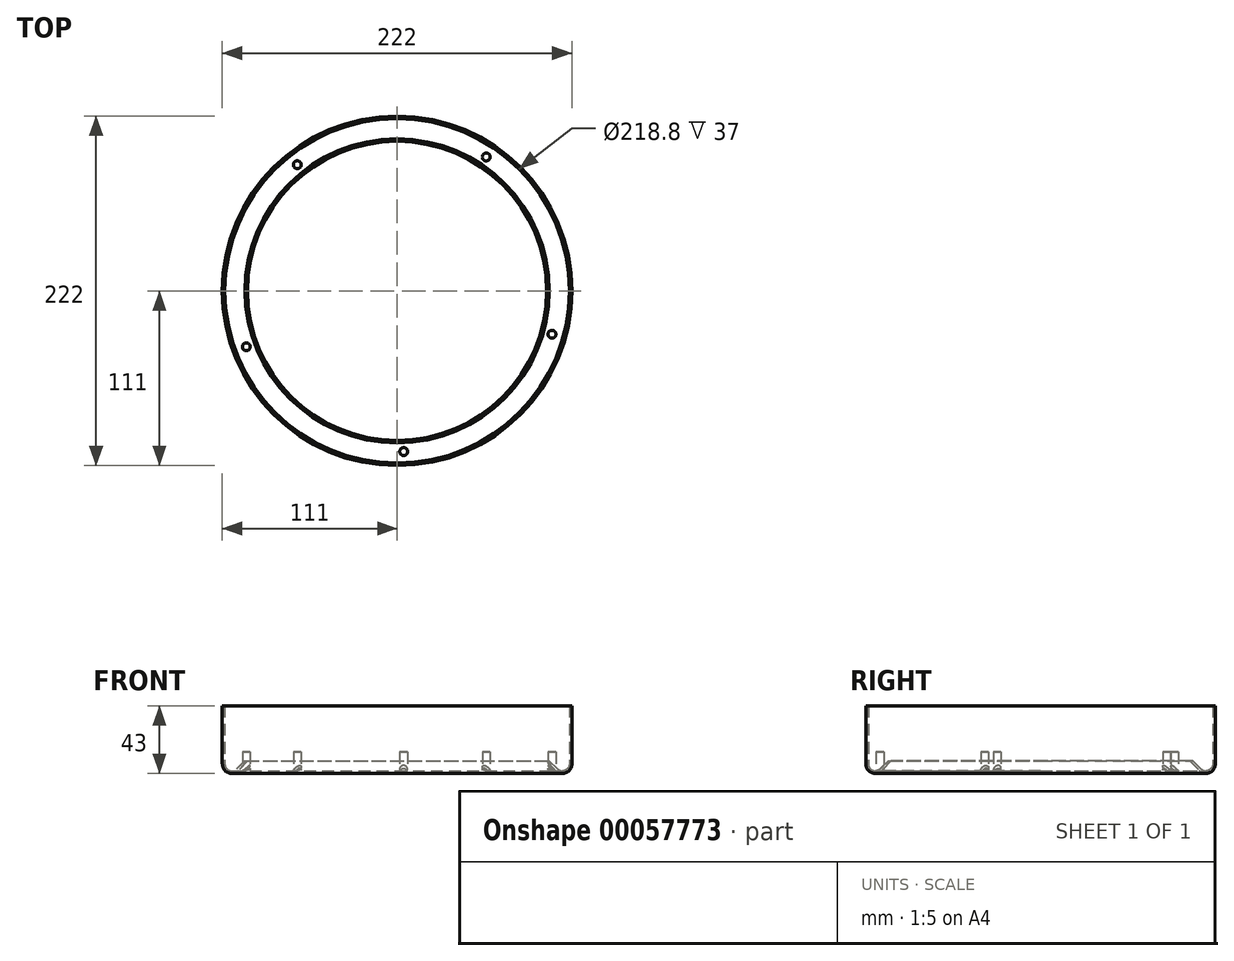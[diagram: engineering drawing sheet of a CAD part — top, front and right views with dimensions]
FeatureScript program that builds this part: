
annotation { "Feature Type Name" : "Feature", "Feature Type Description" : "" }
export const myFeature = defineFeature(function(context is Context, id is Id, definition is map)
    precondition{}
    {
        {
            var Q0;
            Q0=qCreatedBy(makeId("Front.planeOp"),FACE);
            var sketch = newSketch(context, id + "F0", { "sketchPlane" : qUnion([Q0])});
            skLineSegment(sketch, "E0", {"start": v(0, 0) * mm, "end": v(0, 29.4) * mm});
            skLineSegment(sketch, "E1.0", {"start": v(111, 6.44) * mm, "end": v(111, 43.44) * mm});
            skLineSegment(sketch, "E2.0", {"start": v(95, 8.44) * mm, "end": v(96.6, 8.44) * mm});
            skLineSegment(sketch, "E3.0", {"start": v(109.4, 6.44) * mm, "end": v(109.4, 43.44) * mm});
            skArc(sketch, "E4.filletArc", {"start": v(105, 2.04) * mm, "mid": v(108.11, 3.33) * mm, "end": v(109.4, 6.44) * mm});
            skArc(sketch, "E5.filletArc", {"start": v(105, 0.44) * mm, "mid": v(109.24, 2.2) * mm, "end": v(111, 6.44) * mm});
            skArc(sketch, "E6.MirrorCS", {"start": v(105, 2.04) * mm, "mid": v(103.35, 2.36) * mm, "end": v(101.94, 3.27) * mm});
            skArc(sketch, "E7.MirrorCS", {"start": v(105, 0.44) * mm, "mid": v(102.6, 0.94) * mm, "end": v(100.59, 2.37) * mm});
            skLineSegment(sketch, "E8", {"start": v(95, 8.44) * mm, "end": v(100.59, 2.37) * mm});
            skLineSegment(sketch, "E9", {"start": v(96.6, 8.44) * mm, "end": v(101.94, 3.27) * mm});
            skLineSegment(sketch, "E10", {"start": v(111, 43.44) * mm, "end": v(109.4, 43.44) * mm});
            skSolve(sketch);
        }
        {
            var Q0;
            Q0=makeQuery(id+"F0.imprint","IMPRINT",FACE,{"disambiguationData":[TD([[makeQuery(id+"F0.imprint","IMPRINT",EDGE,{"derivedFrom":sQuery(id+"F0.wireOp",EDGE,"E1.0")}),1.0]])]});
            var Q1;
            Q1=sQuery(id+"F0.wireOp",EDGE,"E0");
            revolve(context, id + "F1", {"entities" : qUnion([Q0]), "axis" : qUnion([Q1]), "revolveType" : RevolveType.FULL});
        }
        {
            var Q0;
            Q0=qCreatedBy(makeId("Top.planeOp"),FACE);
            var sketch = newSketch(context, id + "F2", { "sketchPlane" : qUnion([Q0])});
            skCircle(sketch, "E11.cCircle", {"center": v(0, 0) * mm, "radius": 102.16 * mm, "construction": true});
            skLineSegment(sketch, "E11.0", {"start": v(56.61, 85.04) * mm, "end": v(98.38, -27.56) * mm});
            skLineSegment(sketch, "E11.1", {"start": v(98.38, -27.56) * mm, "end": v(4.19, -102.08) * mm});
            skLineSegment(sketch, "E11.2", {"start": v(4.19, -102.08) * mm, "end": v(-95.79, -35.53) * mm});
            skLineSegment(sketch, "E11.3", {"start": v(-95.79, -35.53) * mm, "end": v(-63.39, 80.12) * mm});
            skLineSegment(sketch, "E11.4", {"start": v(-63.39, 80.12) * mm, "end": v(56.61, 85.04) * mm});
            skCircle(sketch, "E12", {"center": v(56.61, 85.04) * mm, "radius": 2.5 * mm});
            skCircle(sketch, "E13.1.0", {"center": v(-63.39, 80.12) * mm, "radius": 2.5 * mm});
            skCircle(sketch, "E13.2.0", {"center": v(-95.79, -35.53) * mm, "radius": 2.5 * mm});
            skCircle(sketch, "E13.3.0", {"center": v(4.19, -102.08) * mm, "radius": 2.5 * mm});
            skCircle(sketch, "E13.4.0", {"center": v(98.38, -27.56) * mm, "radius": 2.5 * mm});
            skSolve(sketch);
        }
        {
            var Q0;
            {var subQ0=sQuery(id+"F2.wireOp",EDGE,"E11.1");var subQ1=sQuery(id+"F2.wireOp",EDGE,"E11.0");var subQ2=makeQuery(id+"F2.imprint","INTERSECT",VERTEX,{"derivedFrom":[subQ1,subQ0]});Q0=makeQuery(id+"F2.imprint","IMPRINT",FACE,{"disambiguationData":[TD([[makeQuery(id+"F2.imprint","IMPRINT",EDGE,{"disambiguationData":[TD([[subQ2,1.0]])],"derivedFrom":subQ1}),1.0]])]});}
            var Q1;
            {var subQ0=sQuery(id+"F2.wireOp",EDGE,"E11.1");var subQ1=sQuery(id+"F2.wireOp",EDGE,"E11.0");var subQ2=makeQuery(id+"F2.imprint","INTERSECT",VERTEX,{"derivedFrom":[subQ1,subQ0]});Q1=makeQuery(id+"F2.imprint","IMPRINT",FACE,{"disambiguationData":[TD([[makeQuery(id+"F2.imprint","IMPRINT",EDGE,{"disambiguationData":[TD([[subQ2,1.0]])],"derivedFrom":subQ1}),-1.0]])]});}
            var Q2;
            {var subQ0=sQuery(id+"F2.wireOp",EDGE,"E11.2");var subQ1=sQuery(id+"F2.wireOp",EDGE,"E11.1");var subQ2=makeQuery(id+"F2.imprint","INTERSECT",VERTEX,{"derivedFrom":[subQ1,subQ0]});Q2=makeQuery(id+"F2.imprint","IMPRINT",FACE,{"disambiguationData":[TD([[makeQuery(id+"F2.imprint","IMPRINT",EDGE,{"disambiguationData":[TD([[subQ2,1.0]])],"derivedFrom":subQ1}),1.0]])]});}
            var Q3;
            {var subQ0=sQuery(id+"F2.wireOp",EDGE,"E11.2");var subQ1=sQuery(id+"F2.wireOp",EDGE,"E11.1");var subQ2=makeQuery(id+"F2.imprint","INTERSECT",VERTEX,{"derivedFrom":[subQ1,subQ0]});Q3=makeQuery(id+"F2.imprint","IMPRINT",FACE,{"disambiguationData":[TD([[makeQuery(id+"F2.imprint","IMPRINT",EDGE,{"disambiguationData":[TD([[subQ2,1.0]])],"derivedFrom":subQ1}),-1.0]])]});}
            var Q4;
            {var subQ0=sQuery(id+"F2.wireOp",EDGE,"E11.3");var subQ1=sQuery(id+"F2.wireOp",EDGE,"E11.2");var subQ2=makeQuery(id+"F2.imprint","INTERSECT",VERTEX,{"derivedFrom":[subQ1,subQ0]});Q4=makeQuery(id+"F2.imprint","IMPRINT",FACE,{"disambiguationData":[TD([[makeQuery(id+"F2.imprint","IMPRINT",EDGE,{"disambiguationData":[TD([[subQ2,1.0]])],"derivedFrom":subQ1}),1.0]])]});}
            var Q5;
            {var subQ0=sQuery(id+"F2.wireOp",EDGE,"E11.3");var subQ1=sQuery(id+"F2.wireOp",EDGE,"E11.2");var subQ2=makeQuery(id+"F2.imprint","INTERSECT",VERTEX,{"derivedFrom":[subQ1,subQ0]});Q5=makeQuery(id+"F2.imprint","IMPRINT",FACE,{"disambiguationData":[TD([[makeQuery(id+"F2.imprint","IMPRINT",EDGE,{"disambiguationData":[TD([[subQ2,1.0]])],"derivedFrom":subQ1}),-1.0]])]});}
            var Q6;
            {var subQ0=sQuery(id+"F2.wireOp",EDGE,"E11.4");var subQ1=sQuery(id+"F2.wireOp",EDGE,"E11.3");var subQ2=makeQuery(id+"F2.imprint","INTERSECT",VERTEX,{"derivedFrom":[subQ1,subQ0]});Q6=makeQuery(id+"F2.imprint","IMPRINT",FACE,{"disambiguationData":[TD([[makeQuery(id+"F2.imprint","IMPRINT",EDGE,{"disambiguationData":[TD([[subQ2,1.0]])],"derivedFrom":subQ1}),1.0]])]});}
            var Q7;
            {var subQ0=sQuery(id+"F2.wireOp",EDGE,"E11.4");var subQ1=sQuery(id+"F2.wireOp",EDGE,"E11.3");var subQ2=makeQuery(id+"F2.imprint","INTERSECT",VERTEX,{"derivedFrom":[subQ1,subQ0]});Q7=makeQuery(id+"F2.imprint","IMPRINT",FACE,{"disambiguationData":[TD([[makeQuery(id+"F2.imprint","IMPRINT",EDGE,{"disambiguationData":[TD([[subQ2,1.0]])],"derivedFrom":subQ1}),-1.0]])]});}
            var Q8;
            {var subQ0=sQuery(id+"F2.wireOp",EDGE,"E11.4");var subQ1=sQuery(id+"F2.wireOp",EDGE,"E11.0");var subQ2=makeQuery(id+"F2.imprint","INTERSECT",VERTEX,{"derivedFrom":[subQ1,subQ0]});Q8=makeQuery(id+"F2.imprint","IMPRINT",FACE,{"disambiguationData":[TD([[makeQuery(id+"F2.imprint","IMPRINT",EDGE,{"disambiguationData":[TD([[subQ2,-1.0]])],"derivedFrom":subQ1}),-1.0]])]});}
            var Q9;
            {var subQ0=sQuery(id+"F2.wireOp",EDGE,"E11.4");var subQ1=sQuery(id+"F2.wireOp",EDGE,"E11.0");var subQ2=makeQuery(id+"F2.imprint","INTERSECT",VERTEX,{"derivedFrom":[subQ1,subQ0]});Q9=makeQuery(id+"F2.imprint","IMPRINT",FACE,{"disambiguationData":[TD([[makeQuery(id+"F2.imprint","IMPRINT",EDGE,{"disambiguationData":[TD([[subQ2,-1.0]])],"derivedFrom":subQ1}),1.0]])]});}
            var Q10;
            Q10=sQuery(id+"F2.wireOp",EDGE,"E13.1.0");
            var Q11;
            Q11=sQuery(id+"F2.wireOp",EDGE,"E12");
            var Q12;
            Q12=sQuery(id+"F2.wireOp",EDGE,"E13.4.0");
            var Q13;
            Q13=sQuery(id+"F2.wireOp",EDGE,"E13.2.0");
            var Q14;
            Q14=sQuery(id+"F2.wireOp",EDGE,"E13.3.0");
            extrude(context, id + "F3", {"entities" : qUnion([Q0, Q1, Q2, Q3, Q4, Q5, Q6, Q7, Q8, Q9]), "operationType" : NewBodyOperationType.ADD, "surfaceEntities" : qUnion([Q10, Q11, Q12, Q13, Q14]), "depth" : 14 * mm});
        }
        {
            var Q0;
            Q0=makeQuery(id+"F3.opExtrude","CAP_FACE",FACE,{"disambiguationData":[OSD([sQuery(id+"F2.wireOp",EDGE,"E13.4.0")])],"isStart":true});
            var Q1;
            Q1=makeQuery(id+"F3.opExtrude","CAP_FACE",FACE,{"disambiguationData":[OSD([sQuery(id+"F2.wireOp",EDGE,"E13.3.0")])],"isStart":true});
            var Q2;
            Q2=makeQuery(id+"F3.opExtrude","CAP_FACE",FACE,{"disambiguationData":[OSD([sQuery(id+"F2.wireOp",EDGE,"E12")])],"isStart":true});
            var Q3;
            Q3=makeQuery(id+"F3.opExtrude","CAP_FACE",FACE,{"disambiguationData":[OSD([sQuery(id+"F2.wireOp",EDGE,"E13.1.0")])],"isStart":true});
            var Q4;
            Q4=makeQuery(id+"F3.opExtrude","CAP_FACE",FACE,{"disambiguationData":[OSD([sQuery(id+"F2.wireOp",EDGE,"E13.2.0")])],"isStart":true});
            var Q5;
            Q5=makeQuery(id+"F1.opRevolve","SWEPT_FACE",FACE,{"disambiguationData":[OSD([sQuery(id+"F0.wireOp",EDGE,"E5.filletArc"),sQuery(id+"F0.wireOp",EDGE,"E7.MirrorCS")])]});
            var Q6;
            Q6=makeQuery(id+"F1.opRevolve","SWEPT_BODY",BODY,{"disambiguationData":[OSD([sQuery(id+"F0.wireOp",EDGE,"E1.0"),sQuery(id+"F0.wireOp",EDGE,"E2.0"),sQuery(id+"F0.wireOp",EDGE,"E3.0"),sQuery(id+"F0.wireOp",EDGE,"E4.filletArc"),sQuery(id+"F0.wireOp",EDGE,"E5.filletArc"),sQuery(id+"F0.wireOp",EDGE,"E6.MirrorCS"),sQuery(id+"F0.wireOp",EDGE,"E7.MirrorCS"),sQuery(id+"F0.wireOp",EDGE,"E8"),sQuery(id+"F0.wireOp",EDGE,"E9"),sQuery(id+"F0.wireOp",EDGE,"E10")])]});
            var Q7;
            Q7=makeQuery(id+"F1.opRevolve","SWEPT_BODY",BODY,{"disambiguationData":[OSD([sQuery(id+"F0.wireOp",EDGE,"E1.0"),sQuery(id+"F0.wireOp",EDGE,"E2.0"),sQuery(id+"F0.wireOp",EDGE,"E3.0"),sQuery(id+"F0.wireOp",EDGE,"E4.filletArc"),sQuery(id+"F0.wireOp",EDGE,"E5.filletArc"),sQuery(id+"F0.wireOp",EDGE,"E6.MirrorCS"),sQuery(id+"F0.wireOp",EDGE,"E7.MirrorCS"),sQuery(id+"F0.wireOp",EDGE,"E8"),sQuery(id+"F0.wireOp",EDGE,"E9"),sQuery(id+"F0.wireOp",EDGE,"E10")])]});
            extrude(context, id + "F4", {"entities" : qUnion([Q0, Q1, Q2, Q3, Q4]), "operationType" : NewBodyOperationType.REMOVE, "endBound" : BoundingType.UP_TO_SURFACE, "oppositeDirection" : true, "endBoundEntityFace" : qUnion([Q5]), "endBoundEntityBody" : qUnion([Q6]), "depth" : 25 * mm});
        }
    });
